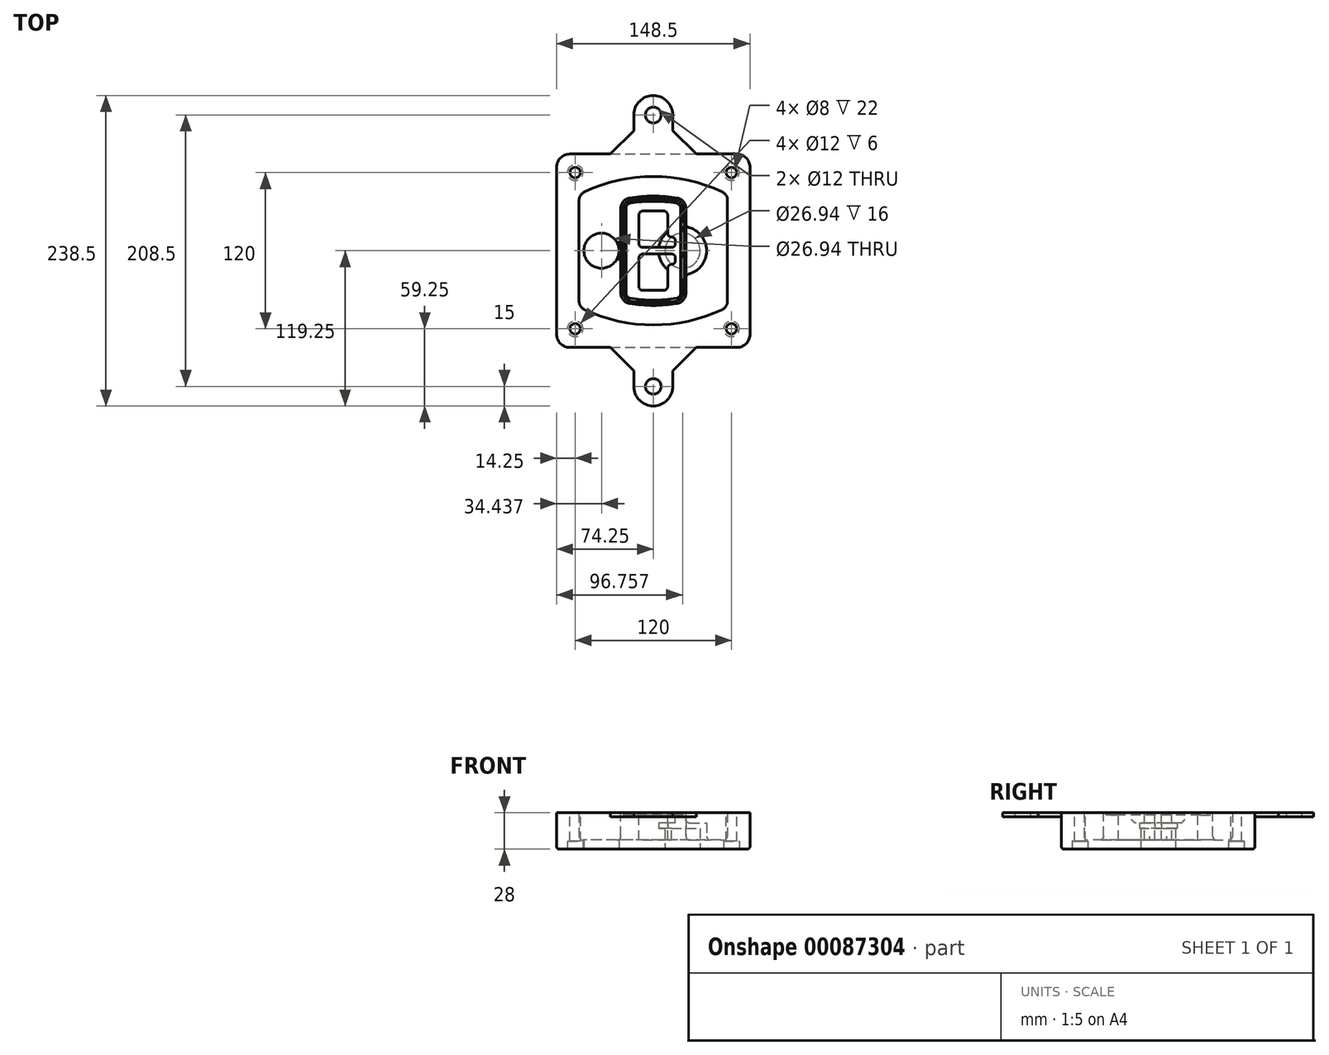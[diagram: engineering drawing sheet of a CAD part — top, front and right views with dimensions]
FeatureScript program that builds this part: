
annotation { "Feature Type Name" : "Feature", "Feature Type Description" : "" }
export const myFeature = defineFeature(function(context is Context, id is Id, definition is map)
    precondition{}
    {
        {
            var Q0;
            Q0=qCreatedBy(makeId("Top.planeOp"),FACE);
            var sketch = newSketch(context, id + "F0", { "sketchPlane" : qUnion([Q0])});
            skPoint(sketch, "E0.rect.middle", {"position": v(0, 0) * mm});
            skLineSegment(sketch, "E1.bottom", {"start": v(-64.25, -74.25) * mm, "end": v(64.25, -74.25) * mm});
            skLineSegment(sketch, "E1.top", {"start": v(-64.25, 74.25) * mm, "end": v(64.25, 74.25) * mm});
            skLineSegment(sketch, "E1.left", {"start": v(-74.25, -64.25) * mm, "end": v(-74.25, 64.25) * mm});
            skLineSegment(sketch, "E1.right", {"start": v(74.25, -64.25) * mm, "end": v(74.25, 64.25) * mm});
            skLineSegment(sketch, "E2", {"start": v(-74.25, 74.25) * mm, "end": v(74.25, -74.25) * mm, "construction": true});
            skLineSegment(sketch, "E3", {"start": v(74.25, 74.25) * mm, "end": v(-74.25, -74.25) * mm, "construction": true});
            skCircle(sketch, "E4", {"center": v(-60, 60) * mm, "radius": 4 * mm});
            skCircle(sketch, "E5", {"center": v(60, 60) * mm, "radius": 4 * mm});
            skCircle(sketch, "E6", {"center": v(60, -60) * mm, "radius": 4 * mm});
            skCircle(sketch, "E7", {"center": v(-60, -60) * mm, "radius": 4 * mm});
            skLineSegment(sketch, "E8", {"start": v(-60, 60) * mm, "end": v(60, 60) * mm, "construction": true});
            skLineSegment(sketch, "E9", {"start": v(60, 60) * mm, "end": v(60, -60) * mm, "construction": true});
            skLineSegment(sketch, "E10", {"start": v(60, -60) * mm, "end": v(-60, -60) * mm, "construction": true});
            skLineSegment(sketch, "E11", {"start": v(-60, -60) * mm, "end": v(-60, 60) * mm, "construction": true});
            skLineSegment(sketch, "E12", {"start": v(-60, 38.83) * mm, "end": v(-60, -38.83) * mm});
            skLineSegment(sketch, "E13", {"start": v(60, 38.83) * mm, "end": v(60, -38.83) * mm});
            skArc(sketch, "E14", {"start": v(54.26, 47.88) * mm, "mid": v(0, 60) * mm, "end": v(-54.26, 47.88) * mm});
            skArc(sketch, "E15", {"start": v(-54.26, -47.88) * mm, "mid": v(0, -60) * mm, "end": v(54.26, -47.88) * mm});
            skLineSegment(sketch, "E16", {"start": v(-60, 0) * mm, "end": v(60, 0) * mm, "construction": true});
            skPoint(sketch, "E17.visualSharp", {"position": v(-60, -45) * mm});
            skArc(sketch, "E17.filletArc", {"start": v(-60, -38.83) * mm, "mid": v(-58.44, -44.2) * mm, "end": v(-54.26, -47.88) * mm});
            skPoint(sketch, "E18.visualSharp", {"position": v(-60, 45) * mm});
            skArc(sketch, "E18.filletArc", {"start": v(-54.26, 47.88) * mm, "mid": v(-58.44, 44.2) * mm, "end": v(-60, 38.83) * mm});
            skPoint(sketch, "E19.visualSharp", {"position": v(60, 45) * mm});
            skArc(sketch, "E19.filletArc", {"start": v(60, 38.83) * mm, "mid": v(58.44, 44.2) * mm, "end": v(54.26, 47.88) * mm});
            skPoint(sketch, "E20.visualSharp", {"position": v(60, -45) * mm});
            skArc(sketch, "E20.filletArc", {"start": v(54.26, -47.88) * mm, "mid": v(58.44, -44.2) * mm, "end": v(60, -38.83) * mm});
            skPoint(sketch, "E21.visualSharp", {"position": v(-74.25, 74.25) * mm});
            skArc(sketch, "E21.filletArc", {"start": v(-64.25, 74.25) * mm, "mid": v(-71.32, 71.32) * mm, "end": v(-74.25, 64.25) * mm});
            skPoint(sketch, "E22.visualSharp", {"position": v(74.25, 74.25) * mm});
            skArc(sketch, "E22.filletArc", {"start": v(74.25, 64.25) * mm, "mid": v(71.32, 71.32) * mm, "end": v(64.25, 74.25) * mm});
            skPoint(sketch, "E23.visualSharp", {"position": v(74.25, -74.25) * mm});
            skArc(sketch, "E23.filletArc", {"start": v(64.25, -74.25) * mm, "mid": v(71.32, -71.32) * mm, "end": v(74.25, -64.25) * mm});
            skPoint(sketch, "E24.visualSharp", {"position": v(-74.25, -74.25) * mm});
            skArc(sketch, "E24.filletArc", {"start": v(-74.25, -64.25) * mm, "mid": v(-71.32, -71.32) * mm, "end": v(-64.25, -74.25) * mm});
            skArc(sketch, "E25.0", {"start": v(57, 38.83) * mm, "mid": v(55.9, 42.58) * mm, "end": v(52.98, 45.17) * mm});
            skLineSegment(sketch, "E25.1", {"start": v(57, 38.83) * mm, "end": v(57, -38.83) * mm});
            skArc(sketch, "E25.2", {"start": v(52.98, -45.17) * mm, "mid": v(55.9, -42.58) * mm, "end": v(57, -38.83) * mm});
            skArc(sketch, "E25.3", {"start": v(-52.98, -45.17) * mm, "mid": v(0, -57) * mm, "end": v(52.98, -45.17) * mm});
            skArc(sketch, "E25.4", {"start": v(-57, -38.83) * mm, "mid": v(-55.9, -42.58) * mm, "end": v(-52.98, -45.17) * mm});
            skArc(sketch, "E25.5", {"start": v(52.98, 45.17) * mm, "mid": v(0, 57) * mm, "end": v(-52.98, 45.17) * mm});
            skLineSegment(sketch, "E25.6", {"start": v(-57, 38.83) * mm, "end": v(-57, -38.83) * mm});
            skArc(sketch, "E25.7", {"start": v(-52.98, 45.17) * mm, "mid": v(-55.9, 42.58) * mm, "end": v(-57, 38.83) * mm});
            skArc(sketch, "E26.0", {"start": v(-55.96, 51.5) * mm, "mid": v(-61.82, 46.33) * mm, "end": v(-64, 38.83) * mm});
            skArc(sketch, "E26.1", {"start": v(55.96, 51.5) * mm, "mid": v(0, 64) * mm, "end": v(-55.96, 51.5) * mm});
            skArc(sketch, "E26.2", {"start": v(64, 38.83) * mm, "mid": v(61.82, 46.33) * mm, "end": v(55.96, 51.5) * mm});
            skLineSegment(sketch, "E26.3", {"start": v(64, 38.83) * mm, "end": v(64, -38.83) * mm});
            skArc(sketch, "E26.4", {"start": v(55.96, -51.5) * mm, "mid": v(61.82, -46.33) * mm, "end": v(64, -38.83) * mm});
            skLineSegment(sketch, "E26.5", {"start": v(-64, 38.83) * mm, "end": v(-64, -38.83) * mm});
            skArc(sketch, "E26.6", {"start": v(-55.96, -51.5) * mm, "mid": v(0, -64) * mm, "end": v(55.96, -51.5) * mm});
            skArc(sketch, "E26.7", {"start": v(-64, -38.83) * mm, "mid": v(-61.82, -46.33) * mm, "end": v(-55.96, -51.5) * mm});
            skSolve(sketch);
        }
        {
            var Q0;
            Q0=makeQuery(id+"F0.imprint","IMPRINT",FACE,{"disambiguationData":[TD([[makeQuery(id+"F0.imprint","IMPRINT",EDGE,{"derivedFrom":sQuery(id+"F0.wireOp",EDGE,"E1.bottom")}),1.0]])]});
            var Q1;
            Q1=makeQuery(id+"F0.imprint","IMPRINT",FACE,{"disambiguationData":[TD([[makeQuery(id+"F0.imprint","IMPRINT",EDGE,{"derivedFrom":sQuery(id+"F0.wireOp",EDGE,"E12")}),1.0]])]});
            var Q2;
            Q2=makeQuery(id+"F0.imprint","IMPRINT",FACE,{"disambiguationData":[TD([[makeQuery(id+"F0.imprint","IMPRINT",EDGE,{"derivedFrom":sQuery(id+"F0.wireOp",EDGE,"E25.0")}),1.0]])]});
            var Q3;
            Q3=makeQuery(id+"F0.imprint","IMPRINT",FACE,{"disambiguationData":[TD([[makeQuery(id+"F0.imprint","IMPRINT",EDGE,{"derivedFrom":sQuery(id+"F0.wireOp",EDGE,"E12")}),-1.0]])]});
            extrude(context, id + "F1", {"entities" : qUnion([Q0, Q1, Q2, Q3]), "oppositeDirection" : true, "depth" : 25 * mm});
        }
        {
            var Q0;
            Q0=makeQuery(id+"F0.imprint","IMPRINT",FACE,{"disambiguationData":[TD([[makeQuery(id+"F0.imprint","IMPRINT",EDGE,{"derivedFrom":sQuery(id+"F0.wireOp",EDGE,"E12")}),1.0]])]});
            extrude(context, id + "F2", {"entities" : qUnion([Q0]), "operationType" : NewBodyOperationType.ADD, "depth" : 3 * mm});
        }
        {
            var Q0;
            Q0=makeQuery(id+"F0.imprint","IMPRINT",FACE,{"disambiguationData":[TD([[makeQuery(id+"F0.imprint","IMPRINT",EDGE,{"derivedFrom":sQuery(id+"F0.wireOp",EDGE,"E25.0")}),1.0]])]});
            extrude(context, id + "F3", {"entities" : qUnion([Q0]), "operationType" : NewBodyOperationType.REMOVE, "oppositeDirection" : true, "depth" : 18 * mm});
        }
        {
            var Q0;
            Q0=makeQuery(id+"F2.opExtrude","CAP_FACE",FACE,{"disambiguationData":[OSD([sQuery(id+"F0.wireOp",EDGE,"E12"),sQuery(id+"F0.wireOp",EDGE,"E13"),sQuery(id+"F0.wireOp",EDGE,"E14"),sQuery(id+"F0.wireOp",EDGE,"E15"),sQuery(id+"F0.wireOp",EDGE,"E17.filletArc"),sQuery(id+"F0.wireOp",EDGE,"E18.filletArc"),sQuery(id+"F0.wireOp",EDGE,"E19.filletArc"),sQuery(id+"F0.wireOp",EDGE,"E20.filletArc"),sQuery(id+"F0.wireOp",EDGE,"E25.0"),sQuery(id+"F0.wireOp",EDGE,"E25.1"),sQuery(id+"F0.wireOp",EDGE,"E25.2"),sQuery(id+"F0.wireOp",EDGE,"E25.3"),sQuery(id+"F0.wireOp",EDGE,"E25.4"),sQuery(id+"F0.wireOp",EDGE,"E25.5"),sQuery(id+"F0.wireOp",EDGE,"E25.6"),sQuery(id+"F0.wireOp",EDGE,"E25.7")])],"isStart":false});
            var sketch = newSketch(context, id + "F4", { "sketchPlane" : qUnion([Q0])});
            skArc(sketch, "E27.0", {"start": v(-18.34, -40.45) * mm, "mid": v(0, -42) * mm, "end": v(18.34, -40.45) * mm});
            skArc(sketch, "E28.0", {"start": v(18.34, 40.45) * mm, "mid": v(0, 42) * mm, "end": v(-18.34, 40.45) * mm});
            skLineSegment(sketch, "E29", {"start": v(-25, 32.57) * mm, "end": v(-25, -32.57) * mm});
            skLineSegment(sketch, "E30", {"start": v(25, 32.57) * mm, "end": v(25, -32.57) * mm});
            skLineSegment(sketch, "E31", {"start": v(-25, 39.1) * mm, "end": v(25, 39.1) * mm, "construction": true});
            skLineSegment(sketch, "E32", {"start": v(-25, -39.1) * mm, "end": v(25, -39.1) * mm, "construction": true});
            skPoint(sketch, "E33.visualSharp", {"position": v(-25, 39.1) * mm});
            skArc(sketch, "E33.filletArc", {"start": v(-18.34, 40.45) * mm, "mid": v(-23.11, 37.73) * mm, "end": v(-25, 32.57) * mm});
            skPoint(sketch, "E34.visualSharp", {"position": v(25, 39.1) * mm});
            skArc(sketch, "E34.filletArc", {"start": v(25, 32.57) * mm, "mid": v(23.11, 37.73) * mm, "end": v(18.34, 40.45) * mm});
            skPoint(sketch, "E35.visualSharp", {"position": v(25, -39.1) * mm});
            skArc(sketch, "E35.filletArc", {"start": v(18.34, -40.45) * mm, "mid": v(23.11, -37.73) * mm, "end": v(25, -32.57) * mm});
            skPoint(sketch, "E36.visualSharp", {"position": v(-25, -39.1) * mm});
            skArc(sketch, "E36.filletArc", {"start": v(-25, -32.57) * mm, "mid": v(-23.11, -37.73) * mm, "end": v(-18.34, -40.45) * mm});
            skArc(sketch, "E37.0", {"start": v(52.98, 45.17) * mm, "mid": v(0, 57) * mm, "end": v(-52.98, 45.17) * mm});
            skArc(sketch, "E37.1", {"start": v(-52.98, 45.17) * mm, "mid": v(-55.9, 42.58) * mm, "end": v(-57, 38.83) * mm});
            skLineSegment(sketch, "E37.2", {"start": v(-57, 38.83) * mm, "end": v(-57, -38.83) * mm});
            skArc(sketch, "E37.3", {"start": v(-57, -38.83) * mm, "mid": v(-55.9, -42.58) * mm, "end": v(-52.98, -45.17) * mm});
            skArc(sketch, "E37.4", {"start": v(-52.98, -45.17) * mm, "mid": v(0, -57) * mm, "end": v(52.98, -45.17) * mm});
            skArc(sketch, "E37.5", {"start": v(52.98, -45.17) * mm, "mid": v(55.9, -42.58) * mm, "end": v(57, -38.83) * mm});
            skLineSegment(sketch, "E37.6", {"start": v(57, 38.83) * mm, "end": v(57, -38.83) * mm});
            skArc(sketch, "E37.7", {"start": v(57, 38.83) * mm, "mid": v(55.9, 42.58) * mm, "end": v(52.98, 45.17) * mm});
            skLineSegment(sketch, "E38.0", {"start": v(23, 32.57) * mm, "end": v(23, -32.57) * mm});
            skArc(sketch, "E38.1", {"start": v(18, -38.48) * mm, "mid": v(21.58, -36.44) * mm, "end": v(23, -32.57) * mm});
            skArc(sketch, "E38.2", {"start": v(-18, -38.48) * mm, "mid": v(0, -40) * mm, "end": v(18, -38.48) * mm});
            skArc(sketch, "E38.3", {"start": v(-23, -32.57) * mm, "mid": v(-21.58, -36.44) * mm, "end": v(-18, -38.48) * mm});
            skLineSegment(sketch, "E38.4", {"start": v(-23, 32.57) * mm, "end": v(-23, -32.57) * mm});
            skArc(sketch, "E38.5", {"start": v(23, 32.57) * mm, "mid": v(21.58, 36.44) * mm, "end": v(18, 38.48) * mm});
            skArc(sketch, "E38.6", {"start": v(-18, 38.48) * mm, "mid": v(-21.58, 36.44) * mm, "end": v(-23, 32.57) * mm});
            skArc(sketch, "E38.7", {"start": v(18, 38.48) * mm, "mid": v(0, 40) * mm, "end": v(-18, 38.48) * mm});
            skArc(sketch, "E39.0", {"start": v(21, 32.57) * mm, "mid": v(20.06, 35.15) * mm, "end": v(17.67, 36.5) * mm});
            skLineSegment(sketch, "E39.1", {"start": v(21, 32.57) * mm, "end": v(21, -32.57) * mm});
            skArc(sketch, "E39.2", {"start": v(17.67, -36.5) * mm, "mid": v(20.06, -35.15) * mm, "end": v(21, -32.57) * mm});
            skArc(sketch, "E39.3", {"start": v(-17.67, -36.5) * mm, "mid": v(0, -38) * mm, "end": v(17.67, -36.5) * mm});
            skArc(sketch, "E39.4", {"start": v(-21, -32.57) * mm, "mid": v(-20.06, -35.15) * mm, "end": v(-17.67, -36.5) * mm});
            skArc(sketch, "E39.5", {"start": v(17.67, 36.5) * mm, "mid": v(0, 38) * mm, "end": v(-17.67, 36.5) * mm});
            skLineSegment(sketch, "E39.6", {"start": v(-21, 32.57) * mm, "end": v(-21, -32.57) * mm});
            skArc(sketch, "E39.7", {"start": v(-17.67, 36.5) * mm, "mid": v(-20.06, 35.15) * mm, "end": v(-21, 32.57) * mm});
            skLineSegment(sketch, "E40", {"start": v(-25, 0) * mm, "end": v(25, 0) * mm, "construction": true});
            skLineSegment(sketch, "E41", {"start": v(-11, 5.5) * mm, "end": v(-11, 27.5) * mm});
            skLineSegment(sketch, "E42", {"start": v(-8, 30.5) * mm, "end": v(8, 30.5) * mm});
            skLineSegment(sketch, "E43", {"start": v(11, 27.5) * mm, "end": v(11, 13.5) * mm});
            skLineSegment(sketch, "E44", {"start": v(14, 10.5) * mm, "end": v(14, 10.5) * mm});
            skLineSegment(sketch, "E45", {"start": v(17, 7.5) * mm, "end": v(17, 5.5) * mm});
            skLineSegment(sketch, "E46", {"start": v(14, 2.5) * mm, "end": v(-8, 2.5) * mm});
            skPoint(sketch, "E47.visualSharp", {"position": v(-11, 30.5) * mm});
            skArc(sketch, "E47.filletArc", {"start": v(-8, 30.5) * mm, "mid": v(-10.12, 29.62) * mm, "end": v(-11, 27.5) * mm});
            skPoint(sketch, "E48.visualSharp", {"position": v(11, 30.5) * mm});
            skArc(sketch, "E48.filletArc", {"start": v(11, 27.5) * mm, "mid": v(10.12, 29.62) * mm, "end": v(8, 30.5) * mm});
            skPoint(sketch, "E49.visualSharp", {"position": v(11, 10.5) * mm});
            skArc(sketch, "E49.filletArc", {"start": v(11, 13.5) * mm, "mid": v(11.88, 11.38) * mm, "end": v(14, 10.5) * mm});
            skPoint(sketch, "E50.visualSharp", {"position": v(17, 10.5) * mm});
            skArc(sketch, "E50.filletArc", {"start": v(17, 7.5) * mm, "mid": v(16.12, 9.62) * mm, "end": v(14, 10.5) * mm});
            skPoint(sketch, "E51.visualSharp", {"position": v(17, 2.5) * mm});
            skArc(sketch, "E51.filletArc", {"start": v(14, 2.5) * mm, "mid": v(16.12, 3.38) * mm, "end": v(17, 5.5) * mm});
            skPoint(sketch, "E52.visualSharp", {"position": v(-11, 2.5) * mm});
            skArc(sketch, "E52.filletArc", {"start": v(-11, 5.5) * mm, "mid": v(-10.12, 3.38) * mm, "end": v(-8, 2.5) * mm});
            skLineSegment(sketch, "E53.0.MirrorCS", {"start": v(14, -2.5) * mm, "end": v(-8, -2.5) * mm});
            skArc(sketch, "E54.0.MirrorCS", {"start": v(-11, -5.5) * mm, "mid": v(-10.12, -3.38) * mm, "end": v(-8, -2.5) * mm});
            skLineSegment(sketch, "E55.0.MirrorCS", {"start": v(-11, -5.5) * mm, "end": v(-11, -27.5) * mm});
            skArc(sketch, "E56.0.MirrorCS", {"start": v(-8, -30.5) * mm, "mid": v(-10.12, -29.62) * mm, "end": v(-11, -27.5) * mm});
            skLineSegment(sketch, "E57.0.MirrorCS", {"start": v(-8, -30.5) * mm, "end": v(8, -30.5) * mm});
            skArc(sketch, "E58.0.MirrorCS", {"start": v(11, -27.5) * mm, "mid": v(10.12, -29.62) * mm, "end": v(8, -30.5) * mm});
            skLineSegment(sketch, "E59.0.MirrorCS", {"start": v(11, -27.5) * mm, "end": v(11, -13.5) * mm});
            skArc(sketch, "E60.0.MirrorCS", {"start": v(11, -13.5) * mm, "mid": v(11.88, -11.38) * mm, "end": v(14, -10.5) * mm});
            skArc(sketch, "E61.0.MirrorCS", {"start": v(17, -7.5) * mm, "mid": v(16.12, -9.62) * mm, "end": v(14, -10.5) * mm});
            skLineSegment(sketch, "E62.0.MirrorCS", {"start": v(17, -7.5) * mm, "end": v(17, -5.5) * mm});
            skArc(sketch, "E63.0.MirrorCS", {"start": v(14, -2.5) * mm, "mid": v(16.12, -3.38) * mm, "end": v(17, -5.5) * mm});
            skSolve(sketch);
        }
        {
            var Q0;
            Q0=makeQuery(id+"F4.imprint","IMPRINT",FACE,{"disambiguationData":[TD([[makeQuery(id+"F4.imprint","IMPRINT",EDGE,{"derivedFrom":sQuery(id+"F4.wireOp",EDGE,"E27.0")}),1.0]])]});
            var Q1;
            Q1=makeQuery(id+"F4.imprint","IMPRINT",FACE,{"disambiguationData":[TD([[makeQuery(id+"F4.imprint","IMPRINT",EDGE,{"derivedFrom":sQuery(id+"F4.wireOp",EDGE,"E38.0")}),-1.0]])]});
            var Q2;
            Q2=makeQuery(id+"F4.imprint","IMPRINT",FACE,{"disambiguationData":[TD([[makeQuery(id+"F4.imprint","IMPRINT",EDGE,{"derivedFrom":sQuery(id+"F4.wireOp",EDGE,"E39.0")}),1.0]])]});
            extrude(context, id + "F5", {"entities" : qUnion([Q0, Q1, Q2]), "operationType" : NewBodyOperationType.ADD, "endBound" : BoundingType.UP_TO_NEXT, "oppositeDirection" : true, "depth" : 25 * mm});
        }
        {
            var Q0;
            Q0=makeQuery(id+"F4.imprint","IMPRINT",FACE,{"disambiguationData":[TD([[makeQuery(id+"F4.imprint","IMPRINT",EDGE,{"derivedFrom":sQuery(id+"F4.wireOp",EDGE,"E38.0")}),-1.0]])]});
            extrude(context, id + "F6", {"entities" : qUnion([Q0]), "operationType" : NewBodyOperationType.REMOVE, "oppositeDirection" : true, "depth" : 2 * mm});
        }
        {
            var Q0;
            Q0=makeQuery(id+"F1.opExtrude","CAP_FACE",FACE,{"disambiguationData":[OSD([sQuery(id+"F0.wireOp",EDGE,"E1.bottom"),sQuery(id+"F0.wireOp",EDGE,"E1.top"),sQuery(id+"F0.wireOp",EDGE,"E1.left"),sQuery(id+"F0.wireOp",EDGE,"E1.right"),sQuery(id+"F0.wireOp",EDGE,"E4"),sQuery(id+"F0.wireOp",EDGE,"E5"),sQuery(id+"F0.wireOp",EDGE,"E6"),sQuery(id+"F0.wireOp",EDGE,"E7"),sQuery(id+"F0.wireOp",EDGE,"E21.filletArc"),sQuery(id+"F0.wireOp",EDGE,"E22.filletArc"),sQuery(id+"F0.wireOp",EDGE,"E23.filletArc"),sQuery(id+"F0.wireOp",EDGE,"E24.filletArc")])],"isStart":false});
            var sketch = newSketch(context, id + "F7", { "sketchPlane" : qUnion([Q0])});
            skCircle(sketch, "E64", {"center": v(22.5, 0) * mm, "radius": 13.47 * mm});
            skCircle(sketch, "E65", {"center": v(-39.81, 0) * mm, "radius": 13.47 * mm});
            skLineSegment(sketch, "E66", {"start": v(74.25, 0) * mm, "end": v(-74.25, 0) * mm});
            skCircle(sketch, "E67", {"center": v(22.5, 0) * mm, "radius": 18.47 * mm});
            skCircle(sketch, "E68", {"center": v(60, -60) * mm, "radius": 6 * mm});
            skCircle(sketch, "E69", {"center": v(-60, -60) * mm, "radius": 6 * mm});
            skCircle(sketch, "E70", {"center": v(-60, 60) * mm, "radius": 6 * mm});
            skCircle(sketch, "E71", {"center": v(60, 60) * mm, "radius": 6 * mm});
            skSolve(sketch);
        }
        {
            var Q0;
            {var subQ1=sQuery(id+"F7.wireOp",EDGE,"E66");var subQ4=sQuery(id+"F7.wireOp",EDGE,"E64");var subQ6=makeQuery(id+"F7.imprint","INTERSECT",VERTEX,{"disambiguationData":[OD(0.0)],"derivedFrom":[subQ4,subQ1]});Q0=makeQuery(id+"F7.imprint","IMPRINT",FACE,{"disambiguationData":[TD([[makeQuery(id+"F7.imprint","IMPRINT",EDGE,{"disambiguationData":[TD([[subQ6,-1.0]])],"derivedFrom":subQ4}),-1.0]])]});}
            var Q1;
            {var subQ0=sQuery(id+"F7.wireOp",EDGE,"E66");var subQ1=sQuery(id+"F7.wireOp",EDGE,"E64");var subQ3=makeQuery(id+"F7.imprint","INTERSECT",VERTEX,{"disambiguationData":[OD(0.0)],"derivedFrom":[subQ1,subQ0]});Q1=makeQuery(id+"F7.imprint","IMPRINT",FACE,{"disambiguationData":[TD([[makeQuery(id+"F7.imprint","IMPRINT",EDGE,{"disambiguationData":[TD([[subQ3,-1.0]])],"derivedFrom":subQ1}),1.0]])]});}
            var Q2;
            {var subQ0=sQuery(id+"F7.wireOp",EDGE,"E66");var subQ1=sQuery(id+"F7.wireOp",EDGE,"E64");var subQ3=makeQuery(id+"F7.imprint","INTERSECT",VERTEX,{"disambiguationData":[OD(0.0)],"derivedFrom":[subQ1,subQ0]});Q2=makeQuery(id+"F7.imprint","IMPRINT",FACE,{"disambiguationData":[TD([[makeQuery(id+"F7.imprint","IMPRINT",EDGE,{"disambiguationData":[TD([[subQ3,1.0]])],"derivedFrom":subQ1}),1.0]])]});}
            var Q3;
            {var subQ1=sQuery(id+"F7.wireOp",EDGE,"E66");var subQ4=sQuery(id+"F7.wireOp",EDGE,"E64");var subQ6=makeQuery(id+"F7.imprint","INTERSECT",VERTEX,{"disambiguationData":[OD(0.0)],"derivedFrom":[subQ4,subQ1]});Q3=makeQuery(id+"F7.imprint","IMPRINT",FACE,{"disambiguationData":[TD([[makeQuery(id+"F7.imprint","IMPRINT",EDGE,{"disambiguationData":[TD([[subQ6,1.0]])],"derivedFrom":subQ4}),-1.0]])]});}
            extrude(context, id + "F8", {"entities" : qUnion([Q0, Q1, Q2, Q3]), "operationType" : NewBodyOperationType.ADD, "oppositeDirection" : true, "depth" : 20 * mm});
        }
        {
            var Q0;
            {var subQ0=sQuery(id+"F7.wireOp",EDGE,"E66");var subQ1=sQuery(id+"F7.wireOp",EDGE,"E64");var subQ3=makeQuery(id+"F7.imprint","INTERSECT",VERTEX,{"disambiguationData":[OD(0.0)],"derivedFrom":[subQ1,subQ0]});Q0=makeQuery(id+"F7.imprint","IMPRINT",FACE,{"disambiguationData":[TD([[makeQuery(id+"F7.imprint","IMPRINT",EDGE,{"disambiguationData":[TD([[subQ3,-1.0]])],"derivedFrom":subQ1}),1.0]])]});}
            var Q1;
            {var subQ0=sQuery(id+"F7.wireOp",EDGE,"E66");var subQ1=sQuery(id+"F7.wireOp",EDGE,"E64");var subQ3=makeQuery(id+"F7.imprint","INTERSECT",VERTEX,{"disambiguationData":[OD(0.0)],"derivedFrom":[subQ1,subQ0]});Q1=makeQuery(id+"F7.imprint","IMPRINT",FACE,{"disambiguationData":[TD([[makeQuery(id+"F7.imprint","IMPRINT",EDGE,{"disambiguationData":[TD([[subQ3,1.0]])],"derivedFrom":subQ1}),1.0]])]});}
            extrude(context, id + "F9", {"entities" : qUnion([Q0, Q1]), "operationType" : NewBodyOperationType.REMOVE, "oppositeDirection" : true, "depth" : 16 * mm});
        }
        {
            var Q0;
            {var subQ0=sQuery(id+"F7.wireOp",EDGE,"E66");var subQ1=sQuery(id+"F7.wireOp",EDGE,"E65");var subQ3=makeQuery(id+"F7.imprint","INTERSECT",VERTEX,{"disambiguationData":[OD(0.0)],"derivedFrom":[subQ1,subQ0]});Q0=makeQuery(id+"F7.imprint","IMPRINT",FACE,{"disambiguationData":[TD([[makeQuery(id+"F7.imprint","IMPRINT",EDGE,{"disambiguationData":[TD([[subQ3,-1.0]])],"derivedFrom":subQ1}),1.0]])]});}
            var Q1;
            {var subQ0=sQuery(id+"F7.wireOp",EDGE,"E66");var subQ1=sQuery(id+"F7.wireOp",EDGE,"E65");var subQ3=makeQuery(id+"F7.imprint","INTERSECT",VERTEX,{"disambiguationData":[OD(0.0)],"derivedFrom":[subQ1,subQ0]});Q1=makeQuery(id+"F7.imprint","IMPRINT",FACE,{"disambiguationData":[TD([[makeQuery(id+"F7.imprint","IMPRINT",EDGE,{"disambiguationData":[TD([[subQ3,1.0]])],"derivedFrom":subQ1}),1.0]])]});}
            extrude(context, id + "F10", {"entities" : qUnion([Q0, Q1]), "operationType" : NewBodyOperationType.REMOVE, "oppositeDirection" : true, "depth" : 25 * mm});
        }
        {
            var Q0;
            Q0=makeQuery(id+"F7.imprint","IMPRINT",FACE,{"disambiguationData":[TD([[makeQuery(id+"F7.imprint","IMPRINT",EDGE,{"derivedFrom":sQuery(id+"F7.wireOp",EDGE,"E68")}),1.0]])]});
            var Q1;
            Q1=makeQuery(id+"F7.imprint","IMPRINT",FACE,{"disambiguationData":[TD([[makeQuery(id+"F7.imprint","IMPRINT",EDGE,{"derivedFrom":makeQuery(id+"F1.opExtrude","CAP_EDGE",EDGE,{"disambiguationData":[OSD([sQuery(id+"F0.wireOp",EDGE,"E5")])],"isStart":false})}),-1.0]])]});
            var Q2;
            Q2=makeQuery(id+"F7.imprint","IMPRINT",FACE,{"disambiguationData":[TD([[makeQuery(id+"F7.imprint","IMPRINT",EDGE,{"derivedFrom":sQuery(id+"F7.wireOp",EDGE,"E69")}),1.0]])]});
            var Q3;
            Q3=makeQuery(id+"F7.imprint","IMPRINT",FACE,{"disambiguationData":[TD([[makeQuery(id+"F7.imprint","IMPRINT",EDGE,{"derivedFrom":makeQuery(id+"F1.opExtrude","CAP_EDGE",EDGE,{"disambiguationData":[OSD([sQuery(id+"F0.wireOp",EDGE,"E4")])],"isStart":false})}),-1.0]])]});
            var Q4;
            Q4=makeQuery(id+"F7.imprint","IMPRINT",FACE,{"disambiguationData":[TD([[makeQuery(id+"F7.imprint","IMPRINT",EDGE,{"derivedFrom":sQuery(id+"F7.wireOp",EDGE,"E70")}),1.0]])]});
            var Q5;
            Q5=makeQuery(id+"F7.imprint","IMPRINT",FACE,{"disambiguationData":[TD([[makeQuery(id+"F7.imprint","IMPRINT",EDGE,{"derivedFrom":makeQuery(id+"F1.opExtrude","CAP_EDGE",EDGE,{"disambiguationData":[OSD([sQuery(id+"F0.wireOp",EDGE,"E7")])],"isStart":false})}),-1.0]])]});
            var Q6;
            Q6=makeQuery(id+"F7.imprint","IMPRINT",FACE,{"disambiguationData":[TD([[makeQuery(id+"F7.imprint","IMPRINT",EDGE,{"derivedFrom":sQuery(id+"F7.wireOp",EDGE,"E71")}),1.0]])]});
            var Q7;
            Q7=makeQuery(id+"F7.imprint","IMPRINT",FACE,{"disambiguationData":[TD([[makeQuery(id+"F7.imprint","IMPRINT",EDGE,{"derivedFrom":makeQuery(id+"F1.opExtrude","CAP_EDGE",EDGE,{"disambiguationData":[OSD([sQuery(id+"F0.wireOp",EDGE,"E6")])],"isStart":false})}),-1.0]])]});
            extrude(context, id + "F11", {"entities" : qUnion([Q0, Q1, Q2, Q3, Q4, Q5, Q6, Q7]), "operationType" : NewBodyOperationType.REMOVE, "oppositeDirection" : true, "depth" : 6 * mm});
        }
        {
            var Q0;
            Q0=makeQuery(id+"F9.boolean.opBoolean","COPY",FACE,{"derivedFrom":makeQuery(id+"F9.opExtrude","CAP_FACE",FACE,{"disambiguationData":[OSD([sQuery(id+"F7.wireOp",EDGE,"E64")])],"isStart":false})});
            var sketch = newSketch(context, id + "F12", { "sketchPlane" : qUnion([Q0])});
            skArc(sketch, "E72.0", {"start": v(11, 14.45) * mm, "mid": v(6.45, 9.13) * mm, "end": v(4.2, 2.5) * mm});
            skArc(sketch, "E72.1", {"start": v(4.2, -2.5) * mm, "mid": v(6.45, -9.13) * mm, "end": v(11, -14.45) * mm});
            skLineSegment(sketch, "E73", {"start": v(4.2, -2.5) * mm, "end": v(14, -2.5) * mm});
            skLineSegment(sketch, "E74.0", {"start": v(14, 2.5) * mm, "end": v(4.2, 2.5) * mm});
            skArc(sketch, "E74.1", {"start": v(14, 2.5) * mm, "mid": v(16.12, 3.38) * mm, "end": v(17, 5.5) * mm});
            skLineSegment(sketch, "E74.2", {"start": v(17, 7.5) * mm, "end": v(17, 5.5) * mm});
            skArc(sketch, "E74.3", {"start": v(17, 7.5) * mm, "mid": v(16.12, 9.62) * mm, "end": v(14, 10.5) * mm});
            skArc(sketch, "E74.4", {"start": v(11, 13.5) * mm, "mid": v(11.88, 11.38) * mm, "end": v(14, 10.5) * mm});
            skLineSegment(sketch, "E74.5", {"start": v(11, 14.45) * mm, "end": v(11, 13.5) * mm});
            skLineSegment(sketch, "E74.7", {"start": v(14, -2.5) * mm, "end": v(4.2, -2.5) * mm});
            skArc(sketch, "E74.8", {"start": v(14, -2.5) * mm, "mid": v(16.12, -3.38) * mm, "end": v(17, -5.5) * mm});
            skLineSegment(sketch, "E74.9", {"start": v(17, -7.5) * mm, "end": v(17, -5.5) * mm});
            skArc(sketch, "E74.10", {"start": v(17, -7.5) * mm, "mid": v(16.12, -9.62) * mm, "end": v(14, -10.5) * mm});
            skArc(sketch, "E74.11", {"start": v(11, -13.5) * mm, "mid": v(11.88, -11.38) * mm, "end": v(14, -10.5) * mm});
            skLineSegment(sketch, "E74.12", {"start": v(11, -14.45) * mm, "end": v(11, -13.5) * mm});
            skPoint(sketch, "E75.orphan", {"position": v(11, -27.5) * mm});
            skPoint(sketch, "E76.orphan", {"position": v(-8, -2.5) * mm});
            skPoint(sketch, "E77.orphan", {"position": v(-8, 2.5) * mm});
            skPoint(sketch, "E78.orphan", {"position": v(11, 27.5) * mm});
            skSolve(sketch);
        }
        {
            var Q0;
            {var subQ7=sQuery(id+"F12.wireOp",EDGE,"E72.0");var subQ14=sQuery(id+"F12.wireOp",EDGE,"E72.1");var subQ16=sQuery(id+"F12.wireOp",EDGE,"E74.1");var subQ18=sQuery(id+"F12.wireOp",EDGE,"E74.8");Q0=qUnion([makeQuery(id+"F12.imprint","IMPRINT",FACE,{"disambiguationData":[TD([[makeQuery(id+"F12.imprint","IMPRINT",EDGE,{"derivedFrom":subQ7}),1.0]])]}),makeQuery(id+"F12.imprint","IMPRINT",FACE,{"disambiguationData":[TD([[makeQuery(id+"F12.imprint","IMPRINT",EDGE,{"derivedFrom":subQ14}),1.0]])]}),makeQuery(id+"F12.imprint","IMPRINT",FACE,{"disambiguationData":[TD([[makeQuery(id+"F12.imprint","IMPRINT",EDGE,{"derivedFrom":subQ16}),1.0]])]}),makeQuery(id+"F12.imprint","IMPRINT",FACE,{"disambiguationData":[TD([[makeQuery(id+"F12.imprint","IMPRINT",EDGE,{"derivedFrom":subQ18}),-1.0]])]})]);}
            var Q1;
            Q1=makeQuery(id+"F5.boolean.opBoolean","SPLIT",FACE,{"disambiguationData":[TD([makeQuery(id+"F5.opExtrude","SWEPT_FACE",FACE,{"disambiguationData":[OSD([sQuery(id+"F4.wireOp",EDGE,"E41")])]})])],"derivedFrom":makeQuery(id+"F3.boolean.opBoolean","COPY",FACE,{"derivedFrom":makeQuery(id+"F3.opExtrude","CAP_FACE",FACE,{"disambiguationData":[OSD([sQuery(id+"F0.wireOp",EDGE,"E25.0"),sQuery(id+"F0.wireOp",EDGE,"E25.1"),sQuery(id+"F0.wireOp",EDGE,"E25.2"),sQuery(id+"F0.wireOp",EDGE,"E25.3"),sQuery(id+"F0.wireOp",EDGE,"E25.4"),sQuery(id+"F0.wireOp",EDGE,"E25.5"),sQuery(id+"F0.wireOp",EDGE,"E25.6"),sQuery(id+"F0.wireOp",EDGE,"E25.7")])],"isStart":false})})});
            extrude(context, id + "F13", {"entities" : qUnion([Q0]), "operationType" : NewBodyOperationType.REMOVE, "endBound" : BoundingType.UP_TO_SURFACE, "endBoundEntityFace" : qUnion([Q1]), "depth" : 25 * mm});
        }
        {
            var Q0;
            Q0=makeQuery(id+"F3.boolean.opBoolean","COPY",EDGE,{"derivedFrom":makeQuery(id+"F3.opExtrude","CAP_EDGE",EDGE,{"disambiguationData":[OSD([sQuery(id+"F0.wireOp",EDGE,"E25.6")])],"isStart":false})});
            var Q1;
            Q1=makeQuery(id+"F8.boolean.opBoolean","INTERSECT",EDGE,{"derivedFrom":[makeQuery(id+"F5.opExtrude","SWEPT_FACE",FACE,{"disambiguationData":[OSD([sQuery(id+"F4.wireOp",EDGE,"E30")])]}),makeQuery(id+"F8.opExtrude","CAP_FACE",FACE,{"disambiguationData":[OSD([sQuery(id+"F7.wireOp",EDGE,"E67")])],"isStart":false})]});
            var Q2;
            Q2=makeQuery(id+"F8.boolean.opBoolean","INTERSECT",EDGE,{"disambiguationData":[OD(1.0)],"derivedFrom":[makeQuery(id+"F5.opExtrude","SWEPT_FACE",FACE,{"disambiguationData":[OSD([sQuery(id+"F4.wireOp",EDGE,"E30")])]}),makeQuery(id+"F8.opExtrude","SWEPT_FACE",FACE,{"disambiguationData":[OSD([sQuery(id+"F7.wireOp",EDGE,"E67")])]})]});
            var Q3;
            {var subQ0=sQuery(id+"F4.wireOp",EDGE,"E30");Q3=makeQuery(id+"F8.boolean.opBoolean","SPLIT",EDGE,{"disambiguationData":[TD([makeQuery(id+"F5.opExtrude","SWEPT_FACE",FACE,{"disambiguationData":[OSD([sQuery(id+"F4.wireOp",EDGE,"E35.filletArc")])]})])],"derivedFrom":makeQuery(id+"F5.opExtrude","CAP_EDGE",EDGE,{"disambiguationData":[OSD([subQ0])],"isStart":false})});}
            var Q4;
            {var subQ0=sQuery(id+"F0.wireOp",EDGE,"E25.7");var subQ1=sQuery(id+"F0.wireOp",EDGE,"E25.1");var subQ2=sQuery(id+"F0.wireOp",EDGE,"E25.6");var subQ3=sQuery(id+"F0.wireOp",EDGE,"E25.5");var subQ4=sQuery(id+"F0.wireOp",EDGE,"E25.4");var subQ5=sQuery(id+"F0.wireOp",EDGE,"E25.0");var subQ6=sQuery(id+"F0.wireOp",EDGE,"E25.2");var subQ7=sQuery(id+"F0.wireOp",EDGE,"E25.3");Q4=makeQuery(id+"F8.boolean.opBoolean","INTERSECT",EDGE,{"derivedFrom":[makeQuery(id+"F5.boolean.opBoolean","SPLIT",FACE,{"disambiguationData":[TD([makeQuery(id+"F2.opExtrude","SWEPT_FACE",FACE,{"disambiguationData":[OSD([subQ5])]})])],"derivedFrom":makeQuery(id+"F3.boolean.opBoolean","COPY",FACE,{"derivedFrom":makeQuery(id+"F3.opExtrude","CAP_FACE",FACE,{"disambiguationData":[OSD([subQ5,subQ1,subQ6,subQ7,subQ4,subQ3,subQ2,subQ0])],"isStart":false})})}),makeQuery(id+"F8.opExtrude","SWEPT_FACE",FACE,{"disambiguationData":[OSD([sQuery(id+"F7.wireOp",EDGE,"E67")])]})]});}
            var Q5;
            Q5=makeQuery(id+"F8.boolean.opBoolean","INTERSECT",EDGE,{"disambiguationData":[OD(0.0)],"derivedFrom":[makeQuery(id+"F5.opExtrude","SWEPT_FACE",FACE,{"disambiguationData":[OSD([sQuery(id+"F4.wireOp",EDGE,"E30")])]}),makeQuery(id+"F8.opExtrude","SWEPT_FACE",FACE,{"disambiguationData":[OSD([sQuery(id+"F7.wireOp",EDGE,"E67")])]})]});
            fillet(context, id + "F14", {"entities" : qUnion([Q0, Q1, Q2, Q3, Q4, Q5]), "radius" : 3 * mm, "tangentPropagation" : true, "allowEdgeOverflow" : false});
        }
        {
            var Q0;
            Q0=makeQuery(id+"F1.opExtrude","CAP_EDGE",EDGE,{"disambiguationData":[OSD([sQuery(id+"F0.wireOp",EDGE,"E1.bottom")])],"isStart":false});
            fillet(context, id + "F15", {"entities" : qUnion([Q0]), "radius" : 2 * mm, "tangentPropagation" : true, "allowEdgeOverflow" : false});
        }
        {
            var Q0;
            {var subQ0=sQuery(id+"F0.wireOp",EDGE,"E22.filletArc");var subQ1=sQuery(id+"F0.wireOp",EDGE,"E7");var subQ2=sQuery(id+"F0.wireOp",EDGE,"E6");var subQ3=sQuery(id+"F0.wireOp",EDGE,"E5");var subQ4=sQuery(id+"F0.wireOp",EDGE,"E4");var subQ5=sQuery(id+"F0.wireOp",EDGE,"E1.bottom");var subQ6=sQuery(id+"F0.wireOp",EDGE,"E21.filletArc");var subQ7=sQuery(id+"F0.wireOp",EDGE,"E1.top");var subQ8=sQuery(id+"F0.wireOp",EDGE,"E1.left");var subQ9=sQuery(id+"F0.wireOp",EDGE,"E1.right");var subQ10=sQuery(id+"F0.wireOp",EDGE,"E23.filletArc");var subQ11=sQuery(id+"F0.wireOp",EDGE,"E24.filletArc");Q0=makeQuery(id+"F2.boolean.opBoolean","SPLIT",FACE,{"disambiguationData":[TD([makeQuery(id+"F1.opExtrude","SWEPT_FACE",FACE,{"disambiguationData":[OSD([subQ5])]})])],"derivedFrom":makeQuery(id+"F1.opExtrude","CAP_FACE",FACE,{"disambiguationData":[OSD([subQ5,subQ7,subQ8,subQ9,subQ4,subQ3,subQ2,subQ1,subQ6,subQ0,subQ10,subQ11])],"isStart":true})});}
            var sketch = newSketch(context, id + "F16", { "sketchPlane" : qUnion([Q0])});
            skLineSegment(sketch, "E79.0", {"start": v(-64.25, 74.25) * mm, "end": v(64.25, 74.25) * mm});
            skLineSegment(sketch, "E80", {"start": v(0, 74.25) * mm, "end": v(0, 104.25) * mm, "construction": true});
            skCircle(sketch, "E81", {"center": v(0, 104.25) * mm, "radius": 6 * mm});
            skArc(sketch, "E82", {"start": v(15, 104.25) * mm, "mid": v(0, 119.25) * mm, "end": v(-15, 104.25) * mm});
            skLineSegment(sketch, "E83", {"start": v(-15, 104.25) * mm, "end": v(-15, 92.25) * mm});
            skLineSegment(sketch, "E84", {"start": v(15, 104.25) * mm, "end": v(15, 92.25) * mm});
            skLineSegment(sketch, "E85", {"start": v(-15, 92.25) * mm, "end": v(-33, 74.25) * mm});
            skLineSegment(sketch, "E86", {"start": v(15, 92.25) * mm, "end": v(33, 74.25) * mm});
            skLineSegment(sketch, "E87", {"start": v(74.25, 0) * mm, "end": v(198.47, 0) * mm, "construction": true});
            skPoint(sketch, "E87.endSnap0", {"position": v(74.25, 0) * mm});
            skLineSegment(sketch, "E88.MirrorCS", {"start": v(15, -104.25) * mm, "end": v(15, -92.25) * mm});
            skArc(sketch, "E89.MirrorCS", {"start": v(15, -104.25) * mm, "mid": v(0, -119.25) * mm, "end": v(-15, -104.25) * mm});
            skLineSegment(sketch, "E90.MirrorCS", {"start": v(-15, -104.25) * mm, "end": v(-15, -92.25) * mm});
            skLineSegment(sketch, "E91.MirrorCS", {"start": v(-15, -92.25) * mm, "end": v(-33, -74.25) * mm});
            skLineSegment(sketch, "E92.MirrorCS", {"start": v(15, -92.25) * mm, "end": v(33, -74.25) * mm});
            skCircle(sketch, "E93.MirrorC", {"center": v(0, -104.25) * mm, "radius": 6 * mm});
            skLineSegment(sketch, "E94.MirrorCS", {"start": v(0, -74.25) * mm, "end": v(0, -104.25) * mm, "construction": true});
            skSolve(sketch);
        }
        {
            var Q0;
            Q0=makeQuery(id+"F16.imprint","IMPRINT",FACE,{"disambiguationData":[TD([[makeQuery(id+"F16.imprint","IMPRINT",EDGE,{"derivedFrom":sQuery(id+"F16.wireOp",EDGE,"E88.MirrorCS")}),1.0]])]});
            var Q1;
            Q1=makeQuery(id+"F16.imprint","IMPRINT",FACE,{"disambiguationData":[TD([[makeQuery(id+"F16.imprint","IMPRINT",EDGE,{"derivedFrom":sQuery(id+"F16.wireOp",EDGE,"E81")}),-1.0]])]});
            var Q2;
            Q2=makeQuery(id+"F16.imprint","IMPRINT",FACE,{"disambiguationData":[TD([[makeQuery(id+"F16.imprint","IMPRINT",EDGE,{"derivedFrom":makeQuery(id+"F1.opExtrude","CAP_EDGE",EDGE,{"disambiguationData":[OSD([sQuery(id+"F0.wireOp",EDGE,"E1.left")])],"isStart":true})}),-1.0]])]});
            var Q3;
            Q3=makeQuery(id+"F2.opExtrude","CAP_FACE",FACE,{"disambiguationData":[OSD([sQuery(id+"F0.wireOp",EDGE,"E12"),sQuery(id+"F0.wireOp",EDGE,"E13"),sQuery(id+"F0.wireOp",EDGE,"E14"),sQuery(id+"F0.wireOp",EDGE,"E15"),sQuery(id+"F0.wireOp",EDGE,"E17.filletArc"),sQuery(id+"F0.wireOp",EDGE,"E18.filletArc"),sQuery(id+"F0.wireOp",EDGE,"E19.filletArc"),sQuery(id+"F0.wireOp",EDGE,"E20.filletArc"),sQuery(id+"F0.wireOp",EDGE,"E25.0"),sQuery(id+"F0.wireOp",EDGE,"E25.1"),sQuery(id+"F0.wireOp",EDGE,"E25.2"),sQuery(id+"F0.wireOp",EDGE,"E25.3"),sQuery(id+"F0.wireOp",EDGE,"E25.4"),sQuery(id+"F0.wireOp",EDGE,"E25.5"),sQuery(id+"F0.wireOp",EDGE,"E25.6"),sQuery(id+"F0.wireOp",EDGE,"E25.7")])],"isStart":false});
            extrude(context, id + "F17", {"entities" : qUnion([Q0, Q1, Q2]), "operationType" : NewBodyOperationType.ADD, "endBound" : BoundingType.UP_TO_SURFACE, "endBoundEntityFace" : qUnion([Q3]), "depth" : 25 * mm});
        }
    });
